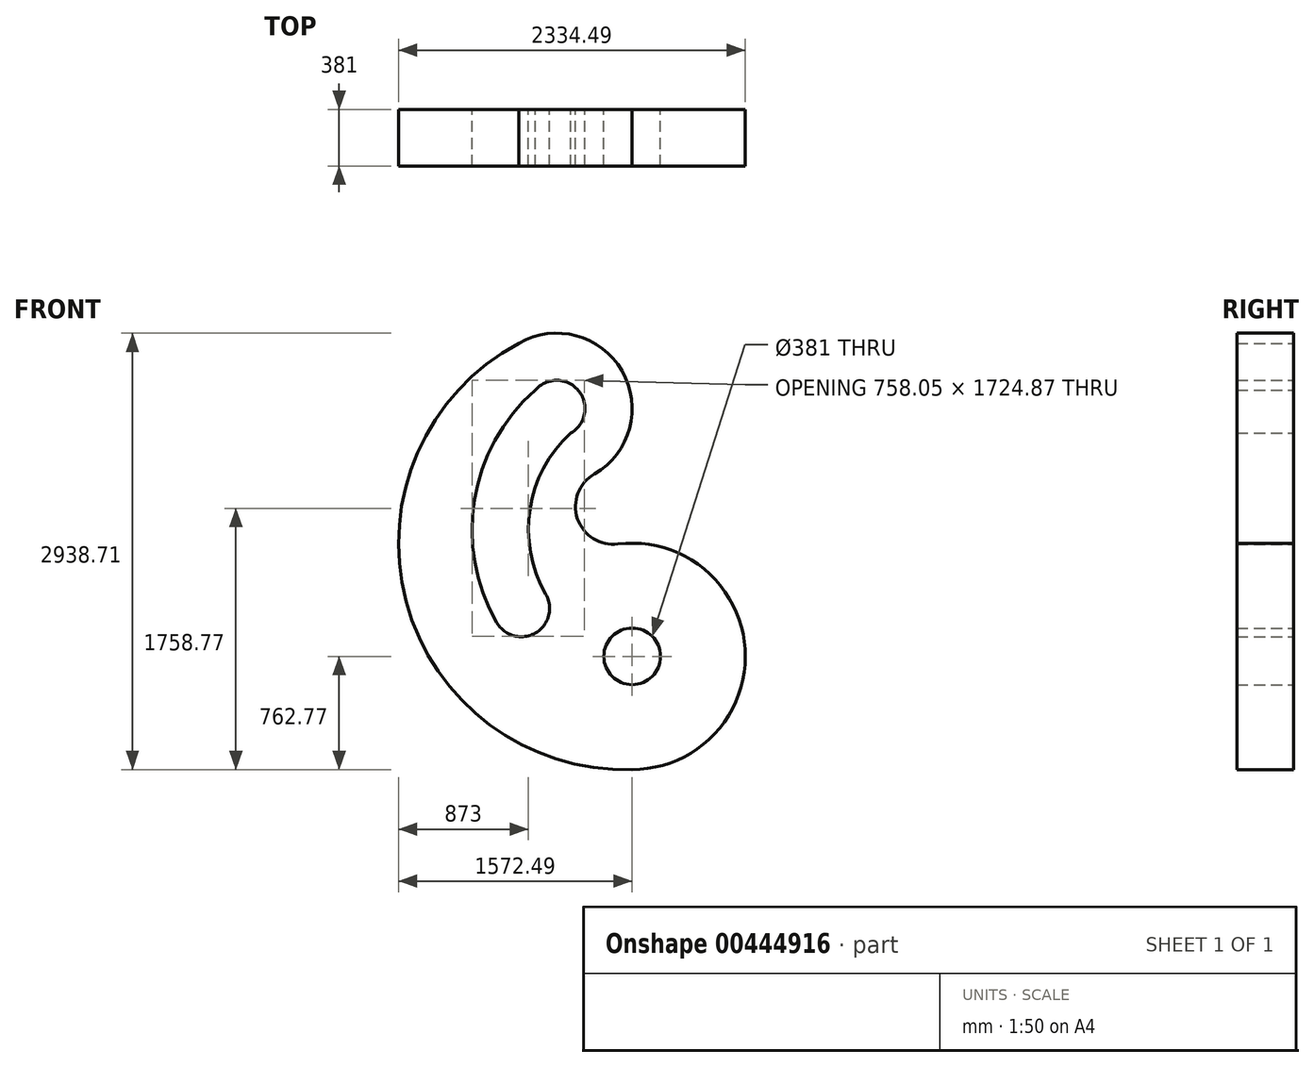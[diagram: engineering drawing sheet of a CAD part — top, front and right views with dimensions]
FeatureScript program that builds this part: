
annotation { "Feature Type Name" : "Feature", "Feature Type Description" : "" }
export const myFeature = defineFeature(function(context is Context, id is Id, definition is map)
    precondition{}
    {
        {
            var Q0;
            Q0=qCreatedBy(makeId("Front.planeOp"),FACE);
            var sketch = newSketch(context, id + "F0", { "sketchPlane" : qUnion([Q0])});
            skCircle(sketch, "E0", {"center": v(0, 0) * mm, "radius": 190.5 * mm});
            skArc(sketch, "E1", {"start": v(0, -762) * mm, "mid": v(760.5, 47.72) * mm, "end": v(-95.25, 756.02) * mm});
            skPoint(sketch, "E2.endSnap0", {"position": v(-254, 983.74) * mm});
            skArc(sketch, "E3", {"start": v(-254, 1228) * mm, "mid": v(-68.06, 1921.94) * mm, "end": v(-762, 2107.88) * mm});
            skArc(sketch, "E4", {"start": v(-254, 1228) * mm, "mid": v(-367.75, 927.06) * mm, "end": v(-95.25, 756.02) * mm});
            skArc(sketch, "E5", {"start": v(-412.75, 1502.96) * mm, "mid": v(-361.57, 1789.8) * mm, "end": v(-652.92, 1791.59) * mm});
            skArc(sketch, "E6", {"start": v(-762, 2107.88) * mm, "mid": v(-1521.45, 370.13) * mm, "end": v(0, -762) * mm});
            skArc(sketch, "E7", {"start": v(-910.94, 227.18) * mm, "mid": v(-630.51, 170.9) * mm, "end": v(-610.34, 456.21) * mm});
            skArc(sketch, "E8", {"start": v(-412.75, 1502.96) * mm, "mid": v(-688.19, 989.98) * mm, "end": v(-580.98, 417.68) * mm});
            skArc(sketch, "E9", {"start": v(-603.25, 1832.92) * mm, "mid": v(-1056.24, 1087.37) * mm, "end": v(-910.94, 227.18) * mm});
            skArc(sketch, "E10.trimOffspring", {"start": v(-605.34, 462.82) * mm, "mid": v(-607.85, 459.52) * mm, "end": v(-610.34, 456.21) * mm});
            skSolve(sketch);
        }
        {
            var Q0;
            Q0=makeQuery(id+"F0.imprint","IMPRINT",FACE,{"disambiguationData":[TD([[makeQuery(id+"F0.imprint","IMPRINT",EDGE,{"derivedFrom":sQuery(id+"F0.wireOp",EDGE,"E0")}),-1.0]])]});
            extrude(context, id + "F1", {"entities" : qUnion([Q0]), "depth" : 381 * mm});
        }
    });
